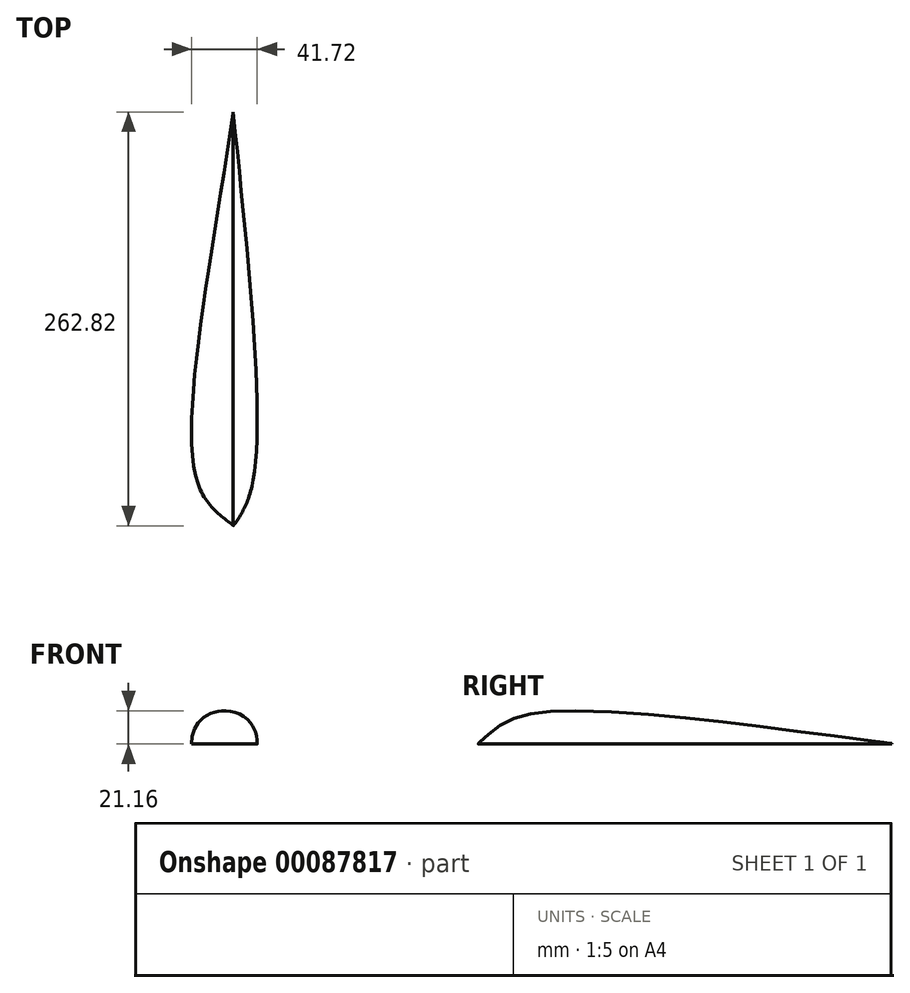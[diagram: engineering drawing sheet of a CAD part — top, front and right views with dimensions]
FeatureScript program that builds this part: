
annotation { "Feature Type Name" : "Feature", "Feature Type Description" : "" }
export const myFeature = defineFeature(function(context is Context, id is Id, definition is map)
    precondition{}
    {
        {
            var Q0;
            Q0=qCreatedBy(makeId("Top.planeOp"),FACE);
            var sketch = newSketch(context, id + "F0", { "sketchPlane" : qUnion([Q0])});
            skLineSegment(sketch, "E0", {"start": v(0, -143.15) * mm, "end": v(0, 210.72) * mm, "construction": true});
            skSolve(sketch);
        }
        {
            var Q0;
            Q0=sQuery(id+"F0.wireOp",EDGE,"E0");
            cPlane(context, id + "F1", {"entities" : qUnion([Q0]), "cplaneType" : CPlaneType.LINE_ANGLE, "offset" : 150 * mm, "angle" : 0.1 * degree, "width" : 150 * mm, "height" : 150 * mm});
        }
        {
            var Q0;
            Q0=qCreatedBy(makeId("Top.planeOp"),FACE);
            var sketch = newSketch(context, id + "F2", { "sketchPlane" : qUnion([Q0])});
            skFitSpline(sketch, "E1", {"points": [v(0, -96) * mm, v(12.73, -66.98) * mm, v(0, 166.8) * mm], "startDerivative": vector(56.05, 79.43) * mm, "endDerivative": vector(-41.09, 397.25) * mm});
            skLineSegment(sketch, "E2", {"start": v(0, -96) * mm, "end": v(0, 166.8) * mm});
            skSolve(sketch);
        }
        {
            var Q0;
            Q0=qCreatedBy(id+"F1.planeOp",FACE);
            var sketch = newSketch(context, id + "F3", { "sketchPlane" : qUnion([Q0])});
            skLineSegment(sketch, "E3", {"start": v(-0.16, -95.8) * mm, "end": v(-0.16, 166) * mm});
            skFitSpline(sketch, "E4", {"points": [v(-0.16, -95.8) * mm, v(-22.45, -69.3) * mm, v(-0.16, 166) * mm], "startDerivative": vector(-80.52, 67.95) * mm, "endDerivative": vector(59.1, 404.05) * mm});
            skSolve(sketch);
        }
        {
            var Q0;
            Q0 = qSketchRegion(id + "F3", true);
            var Q1;
            Q1 = qSketchRegion(id + "F2", true);
            var Q2;
            Q2=sQuery(id+"F3.wireOp",VERTEX,"E4.1.internal");
            var Q3;
            Q3=sQuery(id+"F2.wireOp",VERTEX,"E1.1.internal");
            loft(context, id + "F4", {"startCondition" : LoftEndDerivativeType.NORMAL_TO_PROFILE, "startMagnitude" : 20, "endCondition" : LoftEndDerivativeType.NORMAL_TO_PROFILE, "endMagnitude" : 20, "sheetProfilesArray" : [{ "sheetProfileEntities" : qUnion([Q0]) }, { "sheetProfileEntities" : qUnion([Q1]) }], "matchConnections" : true, "connections" : [{ "connectionEntities" : qUnion([Q2, Q3]), "connectionEdgeQueries" : qUnion([]), "connectionEdgeParameters" : [] }]});
        }
    });
